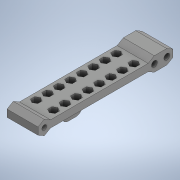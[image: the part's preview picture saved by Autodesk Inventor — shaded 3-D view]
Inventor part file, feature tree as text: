
AUTODESK INVENTOR PART (.ipt)
format: ipt  version: 2020 (Build 240168000, 168)  size: 549,376 bytes
history: native  units: in
note: dims shown in document units (in); Inventor stores cm internally (conversion verified against a paired STEP export)
features: sketch x7, extrude x6, projected_geometry x4, plane x2, mirror x1, fillet x1
ambient origin geometry x8: Origin, YZ Plane, XZ Plane, XY Plane, X Axis, Y Axis, Z Axis, Center Point
bodies: Solid1 (feature_tree)
feature tree (21):
  extrude  "Extrusion1"  Depth=3.4256in
  plane  "Work Plane1"
  extrude  "Extrusion2"  Depth=0.7874in
  sketch  "Sketch4"  dims[d4=0.0in d5=0.0906in]
  extrude  "Extrusion4"  Depth=0.0906in
  plane  "Work Plane2"
  extrude  "Extrusion6"  Depth=3.1106in
  mirror  "Mirror2"
  extrude  "Extrusion7"  Depth=0.315in
  extrude  "Extrusion8"  Depth=0.2362in
  fillet  "Fillet1"  [1 undecoded]
  sketch  "Sketch1"  dims[d0=0.1818in d1=3.4256in]
  sketch  "Sketch2"  dims[d2=0.122in d3=0.7874in]
  sketch  "Sketch5"  dims[d6=0.7874in d7=0.0in d28=3.1106in]
  sketch  "Sketch7"  dims[d29=0.315in d31=0.315in]
  projected_geometry  "Projected Loop7"
  projected_geometry  "Projected Loop8"
  sketch  "Sketch8"  dims[d33=0.1476in d34=0.2362in d35=0.0in]
  projected_geometry  "Projected Loop9"
  sketch  "Sketch10"  dims[d38=0.315in d39=0.2756in d40=-0.3092in d41=0.0787in d42=0.0787in d43=0.0787in d44=3.1496in d46=0.2913in d47=0.3937in d49=0.3937in d51=3.1496in d53=0.2913in d54=0.3937in d56=0.3937in d58=0.0in d59=0.0in d60=1.0994in d61=0.1378in d63=1.1811in d64=0.1575in d65=0.0in d66=0.126in d67=0.1575in]
  projected_geometry  "Projected Loop10"
note: 1 required parameter value undecoded (feature->parameter linkage not recoverable at this tier; creation-order binding heuristic only, values carry confidence <= 0.55)
